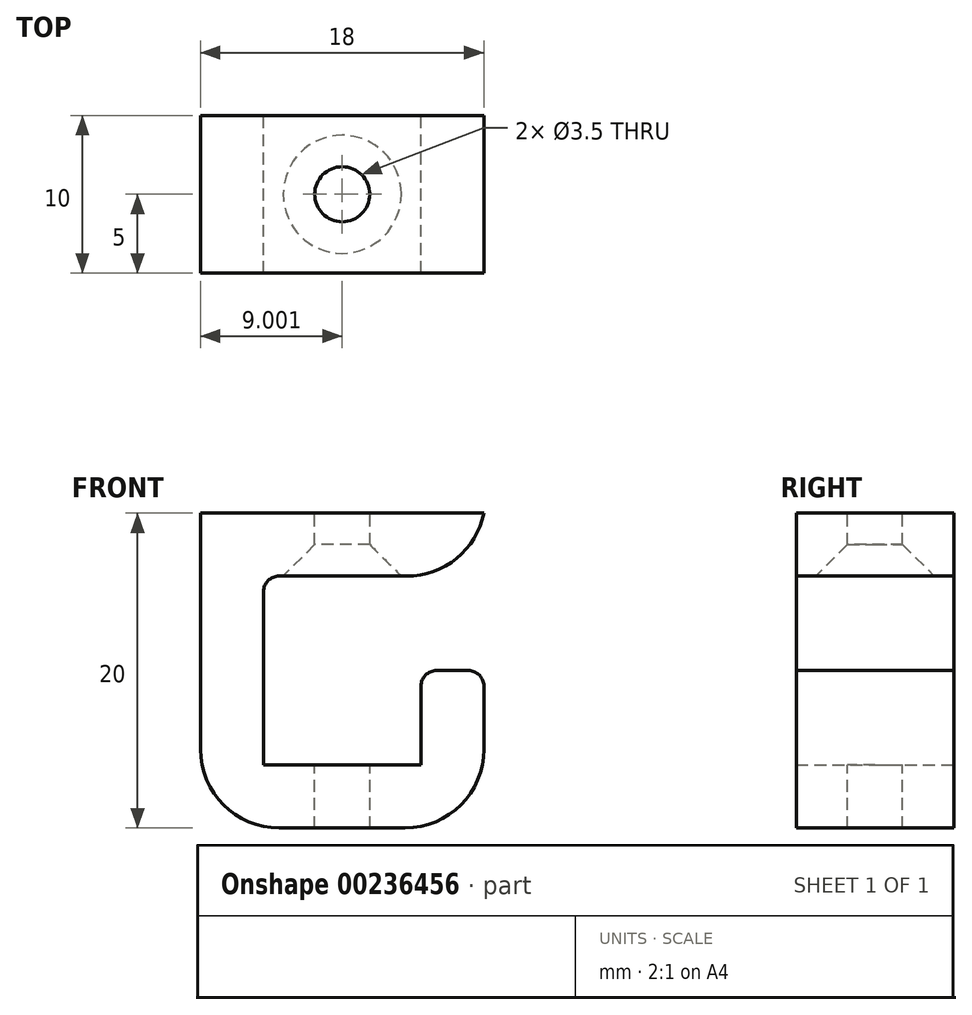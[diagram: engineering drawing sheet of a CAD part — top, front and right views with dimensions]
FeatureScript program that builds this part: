
annotation { "Feature Type Name" : "Feature", "Feature Type Description" : "" }
export const myFeature = defineFeature(function(context is Context, id is Id, definition is map)
    precondition{}
    {
        {
            var Q0;
            Q0=qCreatedBy(makeId("Front.planeOp"),FACE);
            var sketch = newSketch(context, id + "F0", { "sketchPlane" : qUnion([Q0])});
            skLineSegment(sketch, "E0", {"start": v(-18.62, 20) * mm, "end": v(-36.62, 20) * mm});
            skLineSegment(sketch, "E1", {"start": v(-36.62, 20) * mm, "end": v(-36.62, 0) * mm});
            skLineSegment(sketch, "E2", {"start": v(-36.62, 0) * mm, "end": v(-18.62, 0) * mm});
            skLineSegment(sketch, "E3", {"start": v(-18.62, 0) * mm, "end": v(-18.62, 10) * mm});
            skLineSegment(sketch, "E4", {"start": v(-18.62, 10) * mm, "end": v(-22.62, 10) * mm});
            skLineSegment(sketch, "E5", {"start": v(-22.62, 10) * mm, "end": v(-22.62, 4) * mm});
            skLineSegment(sketch, "E6", {"start": v(-22.62, 4) * mm, "end": v(-32.62, 4) * mm});
            skLineSegment(sketch, "E7", {"start": v(-32.62, 4) * mm, "end": v(-32.62, 16) * mm});
            skLineSegment(sketch, "E8", {"start": v(-32.62, 16) * mm, "end": v(-18.62, 16) * mm});
            skLineSegment(sketch, "E9", {"start": v(-18.62, 16) * mm, "end": v(-18.62, 20) * mm});
            skSolve(sketch);
        }
        {
            var Q0;
            Q0=makeQuery(id+"F0.imprint","IMPRINT",FACE,{"disambiguationData":[TD([[makeQuery(id+"F0.imprint","IMPRINT",EDGE,{"derivedFrom":sQuery(id+"F0.wireOp",EDGE,"E0")}),1.0]])]});
            extrude(context, id + "F1", {"entities" : qUnion([Q0]), "depth" : 10 * mm});
        }
        {
            var Q0;
            Q0=makeQuery(id+"F1.opExtrude","SWEPT_EDGE",EDGE,{"disambiguationData":[OSD([sQuery(id+"F0.wireOp",EDGE,"E8"),sQuery(id+"F0.wireOp",EDGE,"E9")])]});
            var Q1;
            Q1=makeQuery(id+"F1.opExtrude","SWEPT_EDGE",EDGE,{"disambiguationData":[OSD([sQuery(id+"F0.wireOp",EDGE,"E2"),sQuery(id+"F0.wireOp",EDGE,"E3")])]});
            var Q2;
            Q2=makeQuery(id+"F1.opExtrude","SWEPT_EDGE",EDGE,{"disambiguationData":[OSD([sQuery(id+"F0.wireOp",EDGE,"E1"),sQuery(id+"F0.wireOp",EDGE,"E2")])]});
            fillet(context, id + "F2", {"entities" : qUnion([Q0, Q1, Q2]), "radius" : 5 * mm, "tangentPropagation" : true, "allowEdgeOverflow" : false});
        }
        {
            var Q0;
            Q0=makeQuery(id+"F1.opExtrude","SWEPT_EDGE",EDGE,{"disambiguationData":[OSD([sQuery(id+"F0.wireOp",EDGE,"E3"),sQuery(id+"F0.wireOp",EDGE,"E4")])]});
            var Q1;
            Q1=makeQuery(id+"F1.opExtrude","SWEPT_EDGE",EDGE,{"disambiguationData":[OSD([sQuery(id+"F0.wireOp",EDGE,"E4"),sQuery(id+"F0.wireOp",EDGE,"E5")])]});
            var Q2;
            Q2=makeQuery(id+"F1.opExtrude","SWEPT_EDGE",EDGE,{"disambiguationData":[OSD([sQuery(id+"F0.wireOp",EDGE,"E7"),sQuery(id+"F0.wireOp",EDGE,"E8")])]});
            fillet(context, id + "F3", {"entities" : qUnion([Q0, Q1, Q2]), "radius" : 1 * mm, "tangentPropagation" : true, "allowEdgeOverflow" : false});
        }
        {
            var Q0;
            Q0=makeQuery(id+"F1.opExtrude","SWEPT_FACE",FACE,{"disambiguationData":[OSD([sQuery(id+"F0.wireOp",EDGE,"E0")])]});
            var sketch = newSketch(context, id + "F4", { "sketchPlane" : qUnion([Q0])});
            skCircle(sketch, "E10", {"center": v(-27.62, -5) * mm, "radius": 1.75 * mm});
            skSolve(sketch);
        }
        {
            var Q0;
            Q0=makeQuery(id+"F4.imprint","IMPRINT",FACE,{"disambiguationData":[TD([[makeQuery(id+"F4.imprint","IMPRINT",EDGE,{"derivedFrom":sQuery(id+"F4.wireOp",EDGE,"E10")}),1.0]])]});
            extrude(context, id + "F5", {"entities" : qUnion([Q0]), "operationType" : NewBodyOperationType.REMOVE, "endBound" : BoundingType.THROUGH_ALL, "oppositeDirection" : true, "depth" : 25 * mm});
        }
        {
            var Q0;
            Q0=makeQuery(id+"F5.boolean.opBoolean","COPY",EDGE,{"derivedFrom":makeQuery(id+"F5.opExtrude","TWEAK_EDGE",EDGE,{"derivedFrom":[makeQuery(id+"F1.opExtrude","SWEPT_FACE",FACE,{"disambiguationData":[OSD([sQuery(id+"F0.wireOp",EDGE,"E8")])]}),makeQuery(id+"F4.imprint","IMPRINT",EDGE,{"derivedFrom":sQuery(id+"F4.wireOp",EDGE,"E10")})]})});
            var Q1;
            Q1=makeQuery(id+"F5.boolean.opBoolean","INTERSECT",EDGE,{"derivedFrom":[makeQuery(id+"F1.opExtrude","SWEPT_FACE",FACE,{"disambiguationData":[OSD([sQuery(id+"F0.wireOp",EDGE,"E8")])]}),makeQuery(id+"F5.opExtrude","SWEPT_FACE",FACE,{"disambiguationData":[OSD([sQuery(id+"F4.wireOp",EDGE,"E10")])]})]});
            chamfer(context, id + "F6", {"entities" : qUnion([Q0, Q1]), "width" : 2 * mm, "tangentPropagation" : true});
        }
    });
